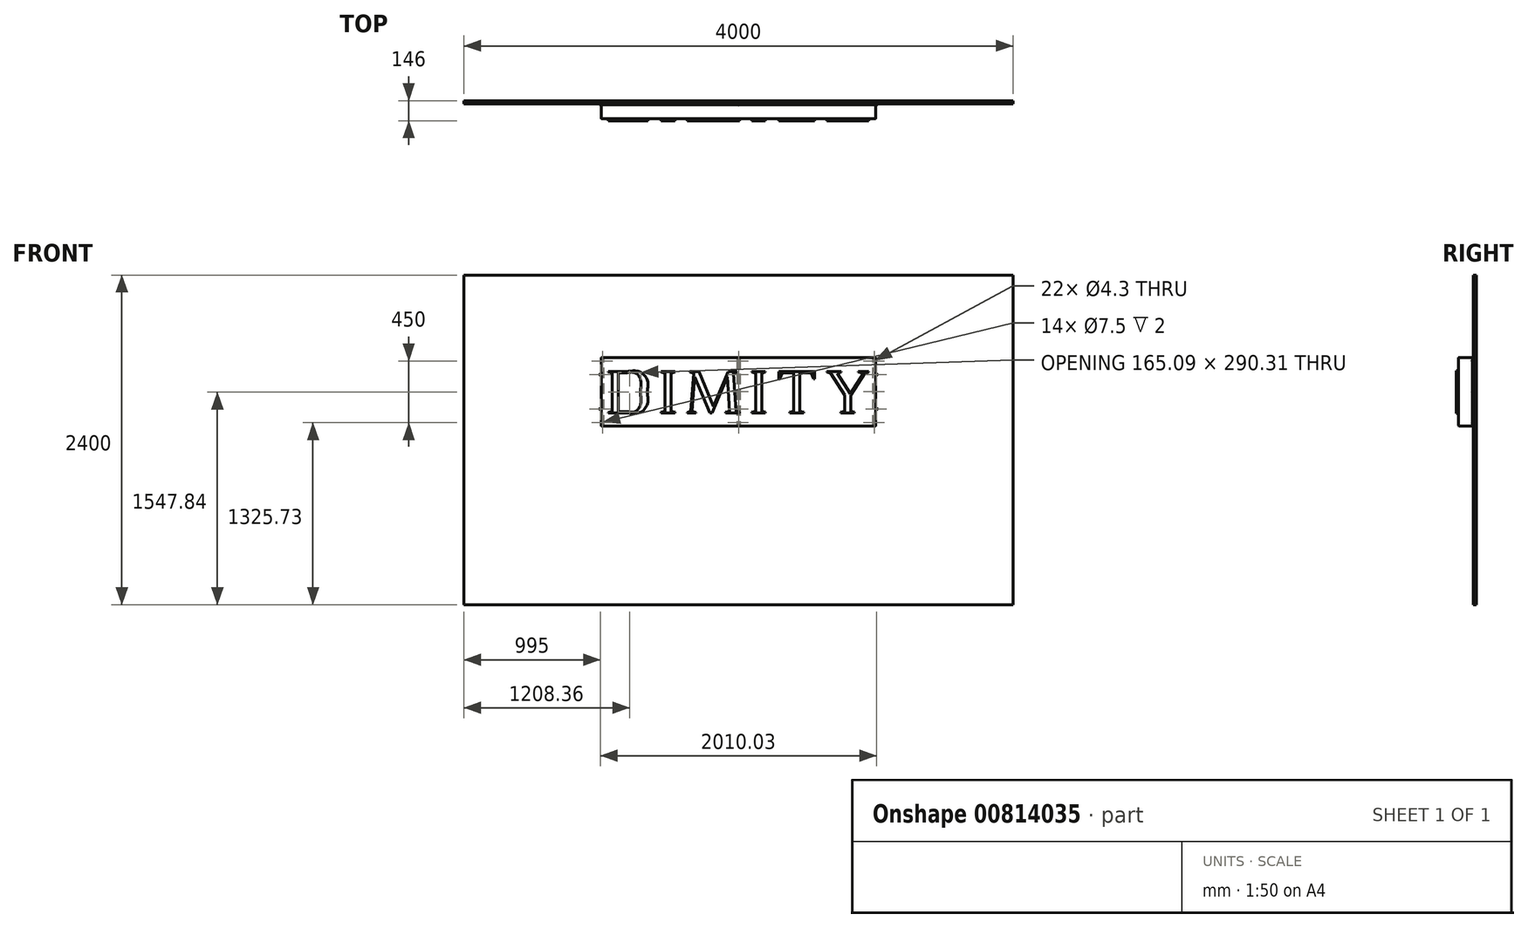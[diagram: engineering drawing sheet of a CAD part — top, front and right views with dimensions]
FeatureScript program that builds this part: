
annotation { "Feature Type Name" : "Feature", "Feature Type Description" : "" }
export const myFeature = defineFeature(function(context is Context, id is Id, definition is map)
    precondition{}
    {
        {
            var Q0;
            Q0=qCreatedBy(makeId("Front.planeOp"),FACE);
            var sketch = newSketch(context, id + "F0", { "sketchPlane" : qUnion([Q0])});
            skLineSegment(sketch, "E0", {"start": v(-948.48, 190.9) * mm, "end": v(-948.48, 187.03) * mm});
            skLineSegment(sketch, "E1", {"start": v(-948.48, 187.03) * mm, "end": v(-920.57, 180.59) * mm});
            skLineSegment(sketch, "E2", {"start": v(-920.57, 180.59) * mm, "end": v(-920.57, -99.41) * mm});
            skLineSegment(sketch, "E3", {"start": v(-920.57, -99.41) * mm, "end": v(-948.48, -106.29) * mm});
            skLineSegment(sketch, "E4", {"start": v(-948.48, -106.29) * mm, "end": v(-948.48, -109.72) * mm});
            skLineSegment(sketch, "E5", {"start": v(-948.48, -109.72) * mm, "end": v(-811.49, -109.72) * mm});
            skFitSpline(sketch, "E6", {"points": [v(-811.49, -109.72) * mm, v(-725.6, -109.72) * mm, v(-665.47, -53.9) * mm, v(-665.47, 40.59) * mm]});
            skFitSpline(sketch, "E7", {"points": [v(-665.47, 40.59) * mm, v(-665.47, 134.2) * mm, v(-725.6, 190.9) * mm, v(-811.49, 190.9) * mm]});
            skLineSegment(sketch, "E8", {"start": v(-811.49, 190.9) * mm, "end": v(-948.48, 190.9) * mm});
            skLineSegment(sketch, "E9", {"start": v(-874.19, 182.3) * mm, "end": v(-811.49, 182.3) * mm});
            skFitSpline(sketch, "E10", {"points": [v(-811.49, 182.3) * mm, v(-754.8, 182.3) * mm, v(-714, 135.07) * mm, v(-714, 40.16) * mm]});
            skFitSpline(sketch, "E11", {"points": [v(-714, 40.16) * mm, v(-714, -54.32) * mm, v(-754.8, -101.13) * mm, v(-811.49, -101.13) * mm]});
            skLineSegment(sketch, "E12", {"start": v(-811.49, -101.13) * mm, "end": v(-874.19, -101.13) * mm});
            skLineSegment(sketch, "E13", {"start": v(-874.19, -101.13) * mm, "end": v(-874.19, 182.3) * mm});
            skLineSegment(sketch, "E14", {"start": v(-563.25, 190.9) * mm, "end": v(-563.25, 186.6) * mm});
            skLineSegment(sketch, "E15", {"start": v(-563.25, 186.6) * mm, "end": v(-535.32, 178.44) * mm});
            skLineSegment(sketch, "E16", {"start": v(-535.32, 178.44) * mm, "end": v(-535.32, -97.27) * mm});
            skLineSegment(sketch, "E17", {"start": v(-535.32, -97.27) * mm, "end": v(-563.25, -105.43) * mm});
            skLineSegment(sketch, "E18", {"start": v(-563.25, -105.43) * mm, "end": v(-563.25, -109.72) * mm});
            skLineSegment(sketch, "E19", {"start": v(-563.25, -109.72) * mm, "end": v(-463.18, -109.72) * mm});
            skLineSegment(sketch, "E20", {"start": v(-463.18, -109.72) * mm, "end": v(-463.18, -105.43) * mm});
            skLineSegment(sketch, "E21", {"start": v(-463.18, -105.43) * mm, "end": v(-489.8, -97.27) * mm});
            skLineSegment(sketch, "E22", {"start": v(-489.8, -97.27) * mm, "end": v(-489.8, 178.44) * mm});
            skLineSegment(sketch, "E23", {"start": v(-489.8, 178.44) * mm, "end": v(-463.18, 186.6) * mm});
            skLineSegment(sketch, "E24", {"start": v(-463.18, 186.6) * mm, "end": v(-463.18, 190.9) * mm});
            skLineSegment(sketch, "E25", {"start": v(-463.18, 190.9) * mm, "end": v(-563.25, 190.9) * mm});
            skLineSegment(sketch, "E26", {"start": v(-354.1, 190.9) * mm, "end": v(-354.1, 186.6) * mm});
            skLineSegment(sketch, "E27", {"start": v(-354.1, 186.6) * mm, "end": v(-326.18, 178.44) * mm});
            skLineSegment(sketch, "E28", {"start": v(-326.18, 178.44) * mm, "end": v(-346.37, -98.13) * mm});
            skLineSegment(sketch, "E29", {"start": v(-346.37, -98.13) * mm, "end": v(-374.28, -106.29) * mm});
            skLineSegment(sketch, "E30", {"start": v(-374.28, -106.29) * mm, "end": v(-374.28, -109.72) * mm});
            skLineSegment(sketch, "E31", {"start": v(-374.28, -109.72) * mm, "end": v(-311.15, -109.72) * mm});
            skLineSegment(sketch, "E32", {"start": v(-311.15, -109.72) * mm, "end": v(-311.15, -106.29) * mm});
            skLineSegment(sketch, "E33", {"start": v(-311.15, -106.29) * mm, "end": v(-337.35, -98.13) * mm});
            skLineSegment(sketch, "E34", {"start": v(-337.35, -98.13) * mm, "end": v(-318.88, 151.82) * mm});
            skLineSegment(sketch, "E35", {"start": v(-318.88, 151.82) * mm, "end": v(-206.8, -109.72) * mm});
            skLineSegment(sketch, "E36", {"start": v(-206.8, -109.72) * mm, "end": v(-192.62, -109.72) * mm});
            skLineSegment(sketch, "E37", {"start": v(-192.62, -109.72) * mm, "end": v(-82.25, 151.39) * mm});
            skLineSegment(sketch, "E38", {"start": v(-82.25, 151.39) * mm, "end": v(-64.21, -97.27) * mm});
            skLineSegment(sketch, "E39", {"start": v(-64.21, -97.27) * mm, "end": v(-92.13, -105.43) * mm});
            skLineSegment(sketch, "E40", {"start": v(-92.13, -105.43) * mm, "end": v(-92.13, -109.72) * mm});
            skLineSegment(sketch, "E41", {"start": v(-92.13, -109.72) * mm, "end": v(8.36, -109.72) * mm});
            skLineSegment(sketch, "E42", {"start": v(8.36, -109.72) * mm, "end": v(8.36, -105.43) * mm});
            skLineSegment(sketch, "E43", {"start": v(8.36, -105.43) * mm, "end": v(-18.27, -97.27) * mm});
            skLineSegment(sketch, "E44", {"start": v(-18.27, -97.27) * mm, "end": v(-38.02, 178.44) * mm});
            skLineSegment(sketch, "E45", {"start": v(-38.02, 178.44) * mm, "end": v(-11.4, 186.6) * mm});
            skLineSegment(sketch, "E46", {"start": v(-11.4, 186.6) * mm, "end": v(-11.4, 190.9) * mm});
            skLineSegment(sketch, "E47", {"start": v(-11.4, 190.9) * mm, "end": v(-74.52, 190.9) * mm});
            skLineSegment(sketch, "E48", {"start": v(-74.52, 190.9) * mm, "end": v(-181.03, -62.48) * mm});
            skLineSegment(sketch, "E49", {"start": v(-181.03, -62.48) * mm, "end": v(-288.39, 190.9) * mm});
            skLineSegment(sketch, "E50", {"start": v(-288.39, 190.9) * mm, "end": v(-354.1, 190.9) * mm});
            skLineSegment(sketch, "E51", {"start": v(96.42, 190.9) * mm, "end": v(96.42, 186.6) * mm});
            skLineSegment(sketch, "E52", {"start": v(96.42, 186.6) * mm, "end": v(124.34, 178.44) * mm});
            skLineSegment(sketch, "E53", {"start": v(124.34, 178.44) * mm, "end": v(124.34, -97.27) * mm});
            skLineSegment(sketch, "E54", {"start": v(124.34, -97.27) * mm, "end": v(96.42, -105.43) * mm});
            skLineSegment(sketch, "E55", {"start": v(96.42, -105.43) * mm, "end": v(96.42, -109.72) * mm});
            skLineSegment(sketch, "E56", {"start": v(96.42, -109.72) * mm, "end": v(196.48, -109.72) * mm});
            skLineSegment(sketch, "E57", {"start": v(196.48, -109.72) * mm, "end": v(196.48, -105.43) * mm});
            skLineSegment(sketch, "E58", {"start": v(196.48, -105.43) * mm, "end": v(169.86, -97.27) * mm});
            skLineSegment(sketch, "E59", {"start": v(169.86, -97.27) * mm, "end": v(169.86, 178.44) * mm});
            skLineSegment(sketch, "E60", {"start": v(169.86, 178.44) * mm, "end": v(196.48, 186.6) * mm});
            skLineSegment(sketch, "E61", {"start": v(196.48, 186.6) * mm, "end": v(196.48, 190.9) * mm});
            skLineSegment(sketch, "E62", {"start": v(196.48, 190.9) * mm, "end": v(96.42, 190.9) * mm});
            skLineSegment(sketch, "E63", {"start": v(293.55, 190.9) * mm, "end": v(293.55, 138.07) * mm});
            skLineSegment(sketch, "E64", {"start": v(293.55, 138.07) * mm, "end": v(300.42, 138.07) * mm});
            skLineSegment(sketch, "E65", {"start": v(300.42, 138.07) * mm, "end": v(320.6, 182.3) * mm});
            skLineSegment(sketch, "E66", {"start": v(320.6, 182.3) * mm, "end": v(400.48, 182.3) * mm});
            skLineSegment(sketch, "E67", {"start": v(400.48, 182.3) * mm, "end": v(400.48, -97.27) * mm});
            skLineSegment(sketch, "E68", {"start": v(400.48, -97.27) * mm, "end": v(372.57, -105.43) * mm});
            skLineSegment(sketch, "E69", {"start": v(372.57, -105.43) * mm, "end": v(372.57, -109.72) * mm});
            skLineSegment(sketch, "E70", {"start": v(372.57, -109.72) * mm, "end": v(474.78, -109.72) * mm});
            skLineSegment(sketch, "E71", {"start": v(474.78, -109.72) * mm, "end": v(474.78, -105.43) * mm});
            skLineSegment(sketch, "E72", {"start": v(474.78, -105.43) * mm, "end": v(446.86, -97.27) * mm});
            skLineSegment(sketch, "E73", {"start": v(446.86, -97.27) * mm, "end": v(446.86, 182.3) * mm});
            skLineSegment(sketch, "E74", {"start": v(446.86, 182.3) * mm, "end": v(527.18, 182.3) * mm});
            skLineSegment(sketch, "E75", {"start": v(527.18, 182.3) * mm, "end": v(546.93, 138.07) * mm});
            skLineSegment(sketch, "E76", {"start": v(546.93, 138.07) * mm, "end": v(554.23, 138.07) * mm});
            skLineSegment(sketch, "E77", {"start": v(554.23, 138.07) * mm, "end": v(554.23, 190.9) * mm});
            skLineSegment(sketch, "E78", {"start": v(554.23, 190.9) * mm, "end": v(293.55, 190.9) * mm});
            skLineSegment(sketch, "E79", {"start": v(644.43, 190.9) * mm, "end": v(644.43, 186.6) * mm});
            skLineSegment(sketch, "E80", {"start": v(644.43, 186.6) * mm, "end": v(671.05, 178.44) * mm});
            skLineSegment(sketch, "E81", {"start": v(671.05, 178.44) * mm, "end": v(771.55, 20.83) * mm});
            skLineSegment(sketch, "E82", {"start": v(771.55, 20.83) * mm, "end": v(771.55, -97.27) * mm});
            skLineSegment(sketch, "E83", {"start": v(771.55, -97.27) * mm, "end": v(743.63, -105.43) * mm});
            skLineSegment(sketch, "E84", {"start": v(743.63, -105.43) * mm, "end": v(743.63, -109.72) * mm});
            skLineSegment(sketch, "E85", {"start": v(743.63, -109.72) * mm, "end": v(844.12, -109.72) * mm});
            skLineSegment(sketch, "E86", {"start": v(844.12, -109.72) * mm, "end": v(844.12, -105.43) * mm});
            skLineSegment(sketch, "E87", {"start": v(844.12, -105.43) * mm, "end": v(817.5, -97.27) * mm});
            skLineSegment(sketch, "E88", {"start": v(817.5, -97.27) * mm, "end": v(817.5, 20.83) * mm});
            skLineSegment(sketch, "E89", {"start": v(817.5, 20.83) * mm, "end": v(917.99, 178.44) * mm});
            skLineSegment(sketch, "E90", {"start": v(917.99, 178.44) * mm, "end": v(948.48, 186.6) * mm});
            skLineSegment(sketch, "E91", {"start": v(948.48, 186.6) * mm, "end": v(948.48, 190.9) * mm});
            skLineSegment(sketch, "E92", {"start": v(948.48, 190.9) * mm, "end": v(872.04, 190.9) * mm});
            skLineSegment(sketch, "E93", {"start": v(872.04, 190.9) * mm, "end": v(872.04, 186.6) * mm});
            skLineSegment(sketch, "E94", {"start": v(872.04, 186.6) * mm, "end": v(908.12, 178.44) * mm});
            skLineSegment(sketch, "E95", {"start": v(908.12, 178.44) * mm, "end": v(813.21, 30.28) * mm});
            skLineSegment(sketch, "E96", {"start": v(813.21, 30.28) * mm, "end": v(719.59, 178.44) * mm});
            skLineSegment(sketch, "E97", {"start": v(719.59, 178.44) * mm, "end": v(747.93, 186.6) * mm});
            skLineSegment(sketch, "E98", {"start": v(747.93, 186.6) * mm, "end": v(747.93, 190.9) * mm});
            skLineSegment(sketch, "E99", {"start": v(747.93, 190.9) * mm, "end": v(644.43, 190.9) * mm});
            skSolve(sketch);
        }
        {
            var Q0;
            Q0=qSketchRegion(id+"F0",true);
            extrude(context, id + "F1", {"entities" : qUnion([Q0]), "depth" : 15 * mm, "offsetDistance" : 25 * mm});
        }
        {
            var Q0;
            Q0=qCreatedBy(makeId("Front.planeOp"),FACE);
            var sketch = newSketch(context, id + "F2", { "sketchPlane" : qUnion([Q0])});
            skLineSegment(sketch, "E100.bottom", {"start": v(1000, 293.5) * mm, "end": v(-1000, 293.5) * mm});
            skLineSegment(sketch, "E100.top", {"start": v(1000, -206.5) * mm, "end": v(-1000, -206.5) * mm});
            skLineSegment(sketch, "E100.left", {"start": v(1000, 293.5) * mm, "end": v(1000, -206.5) * mm});
            skLineSegment(sketch, "E100.right", {"start": v(-1000, 293.5) * mm, "end": v(-1000, -206.5) * mm});
            skLineSegment(sketch, "E101", {"start": v(0, -206.5) * mm, "end": v(-1000, -206.5) * mm, "construction": true});
            skLineSegment(sketch, "E102", {"start": v(-1000, 268.5) * mm, "end": v(1000, 268.5) * mm, "construction": true});
            skLineSegment(sketch, "E103", {"start": v(1000, -181.5) * mm, "end": v(-1000, -181.5) * mm, "construction": true});
            skLineSegment(sketch, "E104", {"start": v(-1000, 43.5) * mm, "end": v(1000, 43.5) * mm, "construction": true});
            skLineSegment(sketch, "E105", {"start": v(0, 293.5) * mm, "end": v(0, -206.5) * mm, "construction": true});
            skLineSegment(sketch, "E106", {"start": v(990, 293.5) * mm, "end": v(990, -206.5) * mm, "construction": true});
            skLineSegment(sketch, "E107", {"start": v(-990, 293.5) * mm, "end": v(-990, -206.5) * mm, "construction": true});
            skSolve(sketch);
        }
        {
            var Q0;
            Q0 = qSketchRegion(id + "F2", true);
            extrude(context, id + "F3", {"entities" : qUnion([Q0]), "oppositeDirection" : true, "depth" : 100 * mm, "offsetDistance" : 25 * mm});
        }
        {
            var Q0;
            Q0=makeQuery(id+"F3.opExtrude","CAP_FACE",FACE,{"disambiguationData":[OSD([sQuery(id+"F2.wireOp",EDGE,"E100.bottom"),sQuery(id+"F2.wireOp",EDGE,"E100.top"),sQuery(id+"F2.wireOp",EDGE,"E100.left"),sQuery(id+"F2.wireOp",EDGE,"E100.right")])],"isStart":false});
            var sketch = newSketch(context, id + "F4", { "sketchPlane" : qUnion([Q0])});
            skLineSegment(sketch, "E108.bottom", {"start": v(-1000, -206.5) * mm, "end": v(-980, -206.5) * mm});
            skLineSegment(sketch, "E108.top", {"start": v(-1000, 293.5) * mm, "end": v(-980, 293.5) * mm});
            skLineSegment(sketch, "E108.left", {"start": v(-1000, -206.5) * mm, "end": v(-1000, 293.5) * mm});
            skLineSegment(sketch, "E108.right", {"start": v(-980, -206.5) * mm, "end": v(-980, 293.5) * mm});
            skLineSegment(sketch, "E109.bottom", {"start": v(-10, 293.5) * mm, "end": v(10, 293.5) * mm});
            skLineSegment(sketch, "E109.top", {"start": v(-10, -206.5) * mm, "end": v(10, -206.5) * mm});
            skLineSegment(sketch, "E109.left", {"start": v(-10, 293.5) * mm, "end": v(-10, -206.5) * mm});
            skLineSegment(sketch, "E109.right", {"start": v(10, 293.5) * mm, "end": v(10, -206.5) * mm});
            skLineSegment(sketch, "E110.MirrorCS", {"start": v(1000, -206.5) * mm, "end": v(980, -206.5) * mm});
            skLineSegment(sketch, "E111.MirrorCS", {"start": v(1000, 293.5) * mm, "end": v(980, 293.5) * mm});
            skLineSegment(sketch, "E112.MirrorCS", {"start": v(980, -206.5) * mm, "end": v(980, 293.5) * mm});
            skLineSegment(sketch, "E113.MirrorCS", {"start": v(1000, -206.5) * mm, "end": v(1000, 293.5) * mm});
            skPoint(sketch, "E114", {"position": v(0, 43.5) * mm});
            skCircle(sketch, "E115", {"center": v(-1000, 168.5) * mm, "radius": 10 * mm});
            skLineSegment(sketch, "E116", {"start": v(-1000, 43.5) * mm, "end": v(1052.48, 43.5) * mm, "construction": true});
            skPoint(sketch, "E116.endSnap0", {"position": v(1000, 43.5) * mm});
            skCircle(sketch, "E117.MirrorC", {"center": v(-1000, -81.5) * mm, "radius": 10 * mm});
            skLineSegment(sketch, "E118", {"start": v(0, -206.5) * mm, "end": v(0, 340.87) * mm, "construction": true});
            skCircle(sketch, "E119.MirrorC", {"center": v(1000, -81.5) * mm, "radius": 10 * mm});
            skCircle(sketch, "E120.MirrorC", {"center": v(1000, 168.5) * mm, "radius": 10 * mm});
            skLineSegment(sketch, "E121", {"start": v(-1000, 168.5) * mm, "end": v(1030.96, 168.5) * mm, "construction": true});
            skLineSegment(sketch, "E122", {"start": v(-1000, -81.5) * mm, "end": v(1050.65, -81.5) * mm, "construction": true});
            skPoint(sketch, "E123", {"position": v(0, -81.5) * mm});
            skPoint(sketch, "E124", {"position": v(0, 168.5) * mm});
            skSolve(sketch);
        }
        {
            var Q0;
            Q0 = qSketchRegion(id + "F4", true);
            extrude(context, id + "F5", {"entities" : qUnion([Q0]), "depth" : 6 * mm, "offsetDistance" : 25 * mm});
        }
        {
            var Q0;
            Q0=makeQuery(id+"F5.opExtrude","CAP_FACE",FACE,{"disambiguationData":[OSD([sQuery(id+"F4.wireOp",EDGE,"E109.bottom"),sQuery(id+"F4.wireOp",EDGE,"E109.top"),sQuery(id+"F4.wireOp",EDGE,"E109.left"),sQuery(id+"F4.wireOp",EDGE,"E109.right")])],"isStart":false});
            var sketch = newSketch(context, id + "F6", { "sketchPlane" : qUnion([Q0])});
            skPoint(sketch, "E125", {"position": v(-990, 268.5) * mm});
            skPoint(sketch, "E126", {"position": v(-990, -181.5) * mm});
            skPoint(sketch, "E127", {"position": v(-990, 43.5) * mm});
            skSolve(sketch);
        }
        {
            var Q0;
            Q0=sQuery(id+"F6.wireOp",VERTEX,"0ecfa253-58d1-4875-90e7-668b1e108a2b1.MirrorP");
            var Q1;
            Q1=sQuery(id+"F6.wireOp",VERTEX,"0ecfa253-58d1-4875-90e7-668b1e108a2b2.MirrorP");
            var Q2;
            Q2=sQuery(id+"F6.wireOp",VERTEX,"0ecfa253-58d1-4875-90e7-668b1e108a2b0.MirrorP");
            var Q3;
            Q3=sQuery(id+"F6.wireOp",VERTEX,"4392e822-1181-4238-817a-814ca760dba6");
            var Q4;
            Q4=sQuery(id+"F6.wireOp",VERTEX,"834a7e99-eb3f-48f6-b097-ef894ec608bc");
            var Q5;
            Q5=sQuery(id+"F6.wireOp",VERTEX,"255140c9-4b28-4841-bfca-1c2cebcfeb9f");
            var Q6;
            Q6=sQuery(id+"F6.wireOp",VERTEX,"E125");
            var Q7;
            Q7=sQuery(id+"F6.wireOp",VERTEX,"E127");
            var Q8;
            Q8=sQuery(id+"F6.wireOp",VERTEX,"E126");
            var Q9;
            Q9=makeQuery(id+"F3.opExtrude","SWEPT_BODY",BODY,{"disambiguationData":[OSD([sQuery(id+"F2.wireOp",EDGE,"E100.bottom"),sQuery(id+"F2.wireOp",EDGE,"E100.top"),sQuery(id+"F2.wireOp",EDGE,"E100.left"),sQuery(id+"F2.wireOp",EDGE,"E100.right")])]});
            var Q10;
            Q10=makeQuery(id+"F5.opExtrude","SWEPT_BODY",BODY,{"disambiguationData":[OSD([sQuery(id+"F4.wireOp",EDGE,"E108.bottom"),sQuery(id+"F4.wireOp",EDGE,"E108.top"),sQuery(id+"F4.wireOp",EDGE,"E108.left"),sQuery(id+"F4.wireOp",EDGE,"E108.right")])]});
            hole(context, id + "F7", {"style" : HoleStyle.C_BORE, "endStyle" : HoleEndStyle.BLIND, "holeDiameter" : 4.3 * mm, "cBoreDiameter" : 7.5 * mm, "cBoreDepth" : 2 * mm, "majorDiameter" : 5 * mm, "holeDepth" : 12 * mm, "isTappedThrough" : true, "tappedDepth" : 12 * mm, "tapClearance" : 3, "startFromSketch" : true, "locations" : qUnion([Q0, Q1, Q2, Q3, Q4, Q5, Q6, Q7, Q8]), "scope" : qUnion([Q9, Q10])});
        }
        {
            var Q0;
            Q0=makeQuery(id+"F5.opExtrude","CAP_FACE",FACE,{"disambiguationData":[OSD([sQuery(id+"F4.wireOp",EDGE,"E109.bottom"),sQuery(id+"F4.wireOp",EDGE,"E109.top"),sQuery(id+"F4.wireOp",EDGE,"E109.left"),sQuery(id+"F4.wireOp",EDGE,"E109.right")])],"isStart":false});
            var sketch = newSketch(context, id + "F8", { "sketchPlane" : qUnion([Q0])});
            skPoint(sketch, "E128", {"position": v(0, 268.5) * mm});
            skPoint(sketch, "E129", {"position": v(0, -181.5) * mm});
            skLineSegment(sketch, "E130", {"start": v(-10, 43.5) * mm, "end": v(-1013.52, 43.5) * mm, "construction": true});
            skLineSegment(sketch, "E131", {"start": v(-1013.52, 43.5) * mm, "end": v(1049.11, 43.5) * mm, "construction": true});
            skPoint(sketch, "E132", {"position": v(0, 43.5) * mm});
            skSolve(sketch);
        }
        {
            var Q0;
            Q0=sQuery(id+"F8.wireOp",VERTEX,"E128");
            var Q1;
            Q1=sQuery(id+"F8.wireOp",VERTEX,"E129");
            var Q2;
            Q2=sQuery(id+"F8.wireOp",VERTEX,"E132");
            var Q3;
            Q3=makeQuery(id+"F3.opExtrude","SWEPT_BODY",BODY,{"disambiguationData":[OSD([sQuery(id+"F2.wireOp",EDGE,"E100.bottom"),sQuery(id+"F2.wireOp",EDGE,"E100.top"),sQuery(id+"F2.wireOp",EDGE,"E100.left"),sQuery(id+"F2.wireOp",EDGE,"E100.right")])]});
            var Q4;
            Q4=makeQuery(id+"F5.opExtrude","SWEPT_BODY",BODY,{"disambiguationData":[OSD([sQuery(id+"F4.wireOp",EDGE,"E109.bottom"),sQuery(id+"F4.wireOp",EDGE,"E109.top"),sQuery(id+"F4.wireOp",EDGE,"E109.left"),sQuery(id+"F4.wireOp",EDGE,"E109.right")])]});
            hole(context, id + "F9", {"style" : HoleStyle.C_BORE, "endStyle" : HoleEndStyle.BLIND, "holeDiameter" : 4.3 * mm, "cBoreDiameter" : 7.5 * mm, "cBoreDepth" : 2 * mm, "majorDiameter" : 5 * mm, "holeDepth" : 12 * mm, "isTappedThrough" : true, "tappedDepth" : 12 * mm, "tapClearance" : 3, "startFromSketch" : true, "locations" : qUnion([Q0, Q1, Q2]), "scope" : qUnion([Q3, Q4])});
        }
        {
            var Q0;
            Q0=makeQuery(id+"F5.opExtrude","CAP_FACE",FACE,{"disambiguationData":[OSD([sQuery(id+"F4.wireOp",EDGE,"E110.MirrorCS"),sQuery(id+"F4.wireOp",EDGE,"E111.MirrorCS"),sQuery(id+"F4.wireOp",EDGE,"E112.MirrorCS"),sQuery(id+"F4.wireOp",EDGE,"E113.MirrorCS")])],"isStart":false});
            var sketch = newSketch(context, id + "F10", { "sketchPlane" : qUnion([Q0])});
            skPoint(sketch, "E133", {"position": v(990, 268.5) * mm});
            skPoint(sketch, "E134", {"position": v(990, -181.5) * mm});
            skLineSegment(sketch, "E135", {"start": v(-992.53, 226) * mm, "end": v(1066.37, 226) * mm, "construction": true});
            skPoint(sketch, "E136", {"position": v(999.48, 226) * mm});
            skSolve(sketch);
        }
        {
            var Q0;
            Q0=sQuery(id+"F10.wireOp",VERTEX,"E133");
            var Q1;
            Q1=sQuery(id+"F10.wireOp",VERTEX,"E134");
            var Q2;
            Q2=makeQuery(id+"F3.opExtrude","SWEPT_BODY",BODY,{"disambiguationData":[OSD([sQuery(id+"F2.wireOp",EDGE,"E100.bottom"),sQuery(id+"F2.wireOp",EDGE,"E100.top"),sQuery(id+"F2.wireOp",EDGE,"E100.left"),sQuery(id+"F2.wireOp",EDGE,"E100.right")])]});
            var Q3;
            Q3=makeQuery(id+"F5.opExtrude","SWEPT_BODY",BODY,{"disambiguationData":[OSD([sQuery(id+"F4.wireOp",EDGE,"E110.MirrorCS"),sQuery(id+"F4.wireOp",EDGE,"E111.MirrorCS"),sQuery(id+"F4.wireOp",EDGE,"E112.MirrorCS"),sQuery(id+"F4.wireOp",EDGE,"E113.MirrorCS")])]});
            hole(context, id + "F11", {"style" : HoleStyle.C_BORE, "endStyle" : HoleEndStyle.BLIND, "holeDiameter" : 4.3 * mm, "cBoreDiameter" : 7.5 * mm, "cBoreDepth" : 2 * mm, "majorDiameter" : 5 * mm, "holeDepth" : 12 * mm, "isTappedThrough" : true, "tappedDepth" : 12 * mm, "tapClearance" : 3, "startFromSketch" : true, "locations" : qUnion([Q0, Q1]), "scope" : qUnion([Q2, Q3])});
        }
        {
            var Q0;
            Q0=makeQuery(id+"F3.opExtrude","SWEPT_EDGE",EDGE,{"disambiguationData":[OSD([sQuery(id+"F2.wireOp",EDGE,"E100.bottom"),sQuery(id+"F2.wireOp",EDGE,"E100.left")])]});
            var Q1;
            Q1=makeQuery(id+"F3.opExtrude","SWEPT_EDGE",EDGE,{"disambiguationData":[OSD([sQuery(id+"F2.wireOp",EDGE,"E100.top"),sQuery(id+"F2.wireOp",EDGE,"E100.left")])]});
            var Q2;
            Q2=makeQuery(id+"F3.opExtrude","SWEPT_EDGE",EDGE,{"disambiguationData":[OSD([sQuery(id+"F2.wireOp",EDGE,"E100.bottom"),sQuery(id+"F2.wireOp",EDGE,"E100.right")])]});
            var Q3;
            Q3=makeQuery(id+"F3.opExtrude","SWEPT_EDGE",EDGE,{"disambiguationData":[OSD([sQuery(id+"F2.wireOp",EDGE,"E100.top"),sQuery(id+"F2.wireOp",EDGE,"E100.right")])]});
            fillet(context, id + "F12", {"entities" : qUnion([Q0, Q1, Q2, Q3]), "radius" : 5 * mm, "tangentPropagation" : true, "allowEdgeOverflow" : false});
        }
        {
            var Q0;
            Q0=makeQuery(id+"F5.opExtrude","SWEPT_EDGE",EDGE,{"disambiguationData":[OSD([sQuery(id+"F4.wireOp",EDGE,"E111.MirrorCS"),sQuery(id+"F4.wireOp",EDGE,"E113.MirrorCS")])]});
            var Q1;
            Q1=makeQuery(id+"F5.opExtrude","SWEPT_EDGE",EDGE,{"disambiguationData":[OSD([sQuery(id+"F2.wireOp",EDGE,"E100.bottom"),sQuery(id+"F4.wireOp",EDGE,"E111.MirrorCS"),sQuery(id+"F4.wireOp",EDGE,"E112.MirrorCS")])]});
            var Q2;
            Q2=makeQuery(id+"F5.opExtrude","SWEPT_EDGE",EDGE,{"disambiguationData":[OSD([sQuery(id+"F2.wireOp",EDGE,"E100.top"),sQuery(id+"F4.wireOp",EDGE,"E110.MirrorCS"),sQuery(id+"F4.wireOp",EDGE,"E112.MirrorCS")])]});
            var Q3;
            Q3=makeQuery(id+"F5.opExtrude","SWEPT_EDGE",EDGE,{"disambiguationData":[OSD([sQuery(id+"F4.wireOp",EDGE,"E110.MirrorCS"),sQuery(id+"F4.wireOp",EDGE,"E113.MirrorCS")])]});
            var Q4;
            Q4=makeQuery(id+"F5.opExtrude","SWEPT_EDGE",EDGE,{"disambiguationData":[OSD([sQuery(id+"F2.wireOp",EDGE,"E100.top"),sQuery(id+"F4.wireOp",EDGE,"E108.bottom"),sQuery(id+"F4.wireOp",EDGE,"E108.right")])]});
            var Q5;
            Q5=makeQuery(id+"F5.opExtrude","SWEPT_EDGE",EDGE,{"disambiguationData":[OSD([sQuery(id+"F4.wireOp",EDGE,"E108.bottom"),sQuery(id+"F4.wireOp",EDGE,"E108.left")])]});
            var Q6;
            Q6=makeQuery(id+"F5.opExtrude","SWEPT_EDGE",EDGE,{"disambiguationData":[OSD([sQuery(id+"F4.wireOp",EDGE,"E108.top"),sQuery(id+"F4.wireOp",EDGE,"E108.left")])]});
            var Q7;
            Q7=makeQuery(id+"F5.opExtrude","SWEPT_EDGE",EDGE,{"disambiguationData":[OSD([sQuery(id+"F2.wireOp",EDGE,"E100.bottom"),sQuery(id+"F4.wireOp",EDGE,"E108.top"),sQuery(id+"F4.wireOp",EDGE,"E108.right")])]});
            fillet(context, id + "F13", {"entities" : qUnion([Q0, Q1, Q2, Q3, Q4, Q5, Q6, Q7]), "radius" : 5 * mm, "tangentPropagation" : true, "allowEdgeOverflow" : false});
        }
        {
            var Q0;
            Q0=makeQuery(id+"F5.opExtrude","SWEPT_EDGE",EDGE,{"disambiguationData":[OSD([sQuery(id+"F2.wireOp",EDGE,"E100.bottom"),sQuery(id+"F4.wireOp",EDGE,"E109.bottom"),sQuery(id+"F4.wireOp",EDGE,"E109.left")])]});
            var Q1;
            Q1=makeQuery(id+"F5.opExtrude","SWEPT_EDGE",EDGE,{"disambiguationData":[OSD([sQuery(id+"F2.wireOp",EDGE,"E100.bottom"),sQuery(id+"F4.wireOp",EDGE,"E109.bottom"),sQuery(id+"F4.wireOp",EDGE,"E109.right")])]});
            var Q2;
            Q2=makeQuery(id+"F5.opExtrude","SWEPT_EDGE",EDGE,{"disambiguationData":[OSD([sQuery(id+"F2.wireOp",EDGE,"E100.top"),sQuery(id+"F4.wireOp",EDGE,"E109.top"),sQuery(id+"F4.wireOp",EDGE,"E109.right")])]});
            var Q3;
            Q3=makeQuery(id+"F5.opExtrude","SWEPT_EDGE",EDGE,{"disambiguationData":[OSD([sQuery(id+"F2.wireOp",EDGE,"E100.top"),sQuery(id+"F4.wireOp",EDGE,"E109.top"),sQuery(id+"F4.wireOp",EDGE,"E109.left")])]});
            fillet(context, id + "F14", {"entities" : qUnion([Q0, Q1, Q2, Q3]), "radius" : 5 * mm, "tangentPropagation" : true, "allowEdgeOverflow" : false});
        }
        {
            var Q0;
            Q0=sQuery(id+"F4.wireOp",VERTEX,"d758e849-db5a-427a-b024-4eb19a2273b2");
            var Q1;
            Q1=sQuery(id+"F4.wireOp",VERTEX,"cc358966-c31c-4dad-9a23-b7b0ff0bc80f");
            var Q2;
            Q2=sQuery(id+"F4.wireOp",VERTEX,"E124");
            var Q3;
            Q3=sQuery(id+"F4.wireOp",VERTEX,"E123");
            var Q4;
            Q4=sQuery(id+"F4.wireOp",VERTEX,"a07292e4-f132-405f-800e-8e075ea845ee");
            var Q5;
            Q5=sQuery(id+"F4.wireOp",VERTEX,"4b03c0d5-2a5c-4f28-9d97-dcb3cdc43e89");
            var Q6;
            Q6=makeQuery(id+"F5.opExtrude","SWEPT_BODY",BODY,{"disambiguationData":[OSD([sQuery(id+"F4.wireOp",EDGE,"E108.bottom"),sQuery(id+"F4.wireOp",EDGE,"E108.top"),sQuery(id+"F4.wireOp",EDGE,"E108.left"),sQuery(id+"F4.wireOp",EDGE,"E108.right"),sQuery(id+"F4.wireOp",EDGE,"E115"),sQuery(id+"F4.wireOp",EDGE,"E117.MirrorC")])]});
            var Q7;
            Q7=makeQuery(id+"F5.opExtrude","SWEPT_BODY",BODY,{"disambiguationData":[OSD([sQuery(id+"F4.wireOp",EDGE,"E109.bottom"),sQuery(id+"F4.wireOp",EDGE,"E109.top"),sQuery(id+"F4.wireOp",EDGE,"E109.left"),sQuery(id+"F4.wireOp",EDGE,"E109.right")])]});
            var Q8;
            Q8=makeQuery(id+"F5.opExtrude","SWEPT_BODY",BODY,{"disambiguationData":[OSD([sQuery(id+"F4.wireOp",EDGE,"E110.MirrorCS"),sQuery(id+"F4.wireOp",EDGE,"E111.MirrorCS"),sQuery(id+"F4.wireOp",EDGE,"E112.MirrorCS"),sQuery(id+"F4.wireOp",EDGE,"E113.MirrorCS"),sQuery(id+"F4.wireOp",EDGE,"E119.MirrorC"),sQuery(id+"F4.wireOp",EDGE,"E120.MirrorC")])]});
            hole(context, id + "F15", {"style" : HoleStyle.C_BORE, "endStyle" : HoleEndStyle.BLIND, "oppositeDirection" : true, "holeDiameter" : 4.3 * mm, "cBoreDiameter" : 7.5 * mm, "cBoreDepth" : 2 * mm, "majorDiameter" : 5 * mm, "holeDepth" : 12 * mm, "isTappedThrough" : true, "tappedDepth" : 12 * mm, "tapClearance" : 3, "startFromSketch" : true, "locations" : qUnion([Q0, Q1, Q2, Q3, Q4, Q5]), "scope" : qUnion([Q6, Q7, Q8])});
        }
        {
            var Q0;
            Q0=makeQuery(id+"F5.opExtrude","CAP_FACE",FACE,{"disambiguationData":[OSD([sQuery(id+"F4.wireOp",EDGE,"E110.MirrorCS"),sQuery(id+"F4.wireOp",EDGE,"E111.MirrorCS"),sQuery(id+"F4.wireOp",EDGE,"E112.MirrorCS"),sQuery(id+"F4.wireOp",EDGE,"E113.MirrorCS"),sQuery(id+"F4.wireOp",EDGE,"E119.MirrorC"),sQuery(id+"F4.wireOp",EDGE,"E120.MirrorC")])],"isStart":true});
            var sketch = newSketch(context, id + "F16", { "sketchPlane" : qUnion([Q0])});
            skPoint(sketch, "E137", {"position": v(-1005, 168.5) * mm});
            skPoint(sketch, "E138", {"position": v(-1005, -81.5) * mm});
            skSolve(sketch);
        }
        {
            var Q0;
            Q0=sQuery(id+"F16.wireOp",VERTEX,"E137");
            var Q1;
            Q1=sQuery(id+"F16.wireOp",VERTEX,"E138");
            var Q2;
            Q2=makeQuery(id+"F5.opExtrude","SWEPT_BODY",BODY,{"disambiguationData":[OSD([sQuery(id+"F4.wireOp",EDGE,"E110.MirrorCS"),sQuery(id+"F4.wireOp",EDGE,"E111.MirrorCS"),sQuery(id+"F4.wireOp",EDGE,"E112.MirrorCS"),sQuery(id+"F4.wireOp",EDGE,"E113.MirrorCS"),sQuery(id+"F4.wireOp",EDGE,"E119.MirrorC"),sQuery(id+"F4.wireOp",EDGE,"E120.MirrorC")])]});
            hole(context, id + "F17", {"style" : HoleStyle.C_BORE, "endStyle" : HoleEndStyle.BLIND, "holeDiameter" : 4.3 * mm, "cBoreDiameter" : 7.5 * mm, "cBoreDepth" : 2 * mm, "majorDiameter" : 5 * mm, "holeDepth" : 12 * mm, "isTappedThrough" : true, "tappedDepth" : 12 * mm, "tapClearance" : 3, "startFromSketch" : true, "locations" : qUnion([Q0, Q1]), "scope" : qUnion([Q2])});
        }
        {
            var Q0;
            Q0=makeQuery(id+"F5.opExtrude","CAP_FACE",FACE,{"disambiguationData":[OSD([sQuery(id+"F4.wireOp",EDGE,"E108.bottom"),sQuery(id+"F4.wireOp",EDGE,"E108.top"),sQuery(id+"F4.wireOp",EDGE,"E108.left"),sQuery(id+"F4.wireOp",EDGE,"E108.right"),sQuery(id+"F4.wireOp",EDGE,"E115"),sQuery(id+"F4.wireOp",EDGE,"E117.MirrorC")])],"isStart":true});
            var sketch = newSketch(context, id + "F18", { "sketchPlane" : qUnion([Q0])});
            skPoint(sketch, "E139", {"position": v(1005, 168.5) * mm});
            skPoint(sketch, "E140", {"position": v(1005.03, -81.5) * mm});
            skSolve(sketch);
        }
        {
            var Q0;
            Q0=sQuery(id+"F18.wireOp",VERTEX,"E139");
            var Q1;
            Q1=sQuery(id+"F18.wireOp",VERTEX,"E140");
            var Q2;
            Q2=makeQuery(id+"F5.opExtrude","SWEPT_BODY",BODY,{"disambiguationData":[OSD([sQuery(id+"F4.wireOp",EDGE,"E108.bottom"),sQuery(id+"F4.wireOp",EDGE,"E108.top"),sQuery(id+"F4.wireOp",EDGE,"E108.left"),sQuery(id+"F4.wireOp",EDGE,"E108.right"),sQuery(id+"F4.wireOp",EDGE,"E115"),sQuery(id+"F4.wireOp",EDGE,"E117.MirrorC")])]});
            hole(context, id + "F19", {"style" : HoleStyle.C_BORE, "endStyle" : HoleEndStyle.BLIND, "holeDiameter" : 4.3 * mm, "cBoreDiameter" : 7.5 * mm, "cBoreDepth" : 2 * mm, "majorDiameter" : 5 * mm, "holeDepth" : 12 * mm, "isTappedThrough" : true, "tappedDepth" : 12 * mm, "tapClearance" : 3, "startFromSketch" : true, "locations" : qUnion([Q0, Q1]), "scope" : qUnion([Q2])});
        }
        {
            var Q0;
            Q0=makeQuery(id+"F3.opExtrude","CAP_EDGE",EDGE,{"disambiguationData":[OSD([sQuery(id+"F2.wireOp",EDGE,"E100.right")])],"isStart":true});
            var Q1;
            Q1=makeQuery(id+"F3.opExtrude","CAP_EDGE",EDGE,{"disambiguationData":[OSD([sQuery(id+"F2.wireOp",EDGE,"E100.bottom")])],"isStart":true});
            fillet(context, id + "F20", {"entities" : qUnion([Q0, Q1]), "radius" : 5 * mm, "tangentPropagation" : true, "allowEdgeOverflow" : false});
        }
        {
            var Q0;
            Q0=makeQuery(id+"F5.opExtrude","CAP_FACE",FACE,{"disambiguationData":[OSD([sQuery(id+"F4.wireOp",EDGE,"E109.bottom"),sQuery(id+"F4.wireOp",EDGE,"E109.top"),sQuery(id+"F4.wireOp",EDGE,"E109.left"),sQuery(id+"F4.wireOp",EDGE,"E109.right")])],"isStart":false});
            var sketch = newSketch(context, id + "F21", { "sketchPlane" : qUnion([Q0])});
            skLineSegment(sketch, "E141.bottom", {"start": v(0, -1507.24) * mm, "end": v(-1000, -1507.24) * mm});
            skLineSegment(sketch, "E141.top", {"start": v(0, 892.76) * mm, "end": v(-1000, 892.76) * mm});
            skLineSegment(sketch, "E141.left", {"start": v(0, -1507.24) * mm, "end": v(0, 892.76) * mm});
            skLineSegment(sketch, "E141.right", {"start": v(-1000, -1507.24) * mm, "end": v(-1000, 892.76) * mm});
            skLineSegment(sketch, "E142.bottom", {"start": v(0, 892.76) * mm, "end": v(1000, 892.76) * mm});
            skLineSegment(sketch, "E142.top", {"start": v(0, -1507.24) * mm, "end": v(1000, -1507.24) * mm});
            skLineSegment(sketch, "E142.left", {"start": v(0, 892.76) * mm, "end": v(0, -1507.24) * mm});
            skLineSegment(sketch, "E142.right", {"start": v(1000, 892.76) * mm, "end": v(1000, -1507.24) * mm});
            skLineSegment(sketch, "E143.bottom", {"start": v(-1000, 892.76) * mm, "end": v(-2000, 892.76) * mm});
            skLineSegment(sketch, "E143.top", {"start": v(-1000, -1507.24) * mm, "end": v(-2000, -1507.24) * mm});
            skLineSegment(sketch, "E143.left", {"start": v(-1000, 892.76) * mm, "end": v(-1000, -1507.24) * mm});
            skLineSegment(sketch, "E143.right", {"start": v(-2000, 892.76) * mm, "end": v(-2000, -1507.24) * mm});
            skLineSegment(sketch, "E144.bottom", {"start": v(1000, 892.76) * mm, "end": v(2000, 892.76) * mm});
            skLineSegment(sketch, "E144.top", {"start": v(1000, -1507.24) * mm, "end": v(2000, -1507.24) * mm});
            skLineSegment(sketch, "E144.right", {"start": v(2000, 892.76) * mm, "end": v(2000, -1507.24) * mm});
            skSolve(sketch);
        }
        {
            var Q0;
            Q0 = qSketchRegion(id + "F21", true);
            extrude(context, id + "F22", {"entities" : qUnion([Q0]), "depth" : 25 * mm, "offsetDistance" : 25 * mm});
        }
    });
